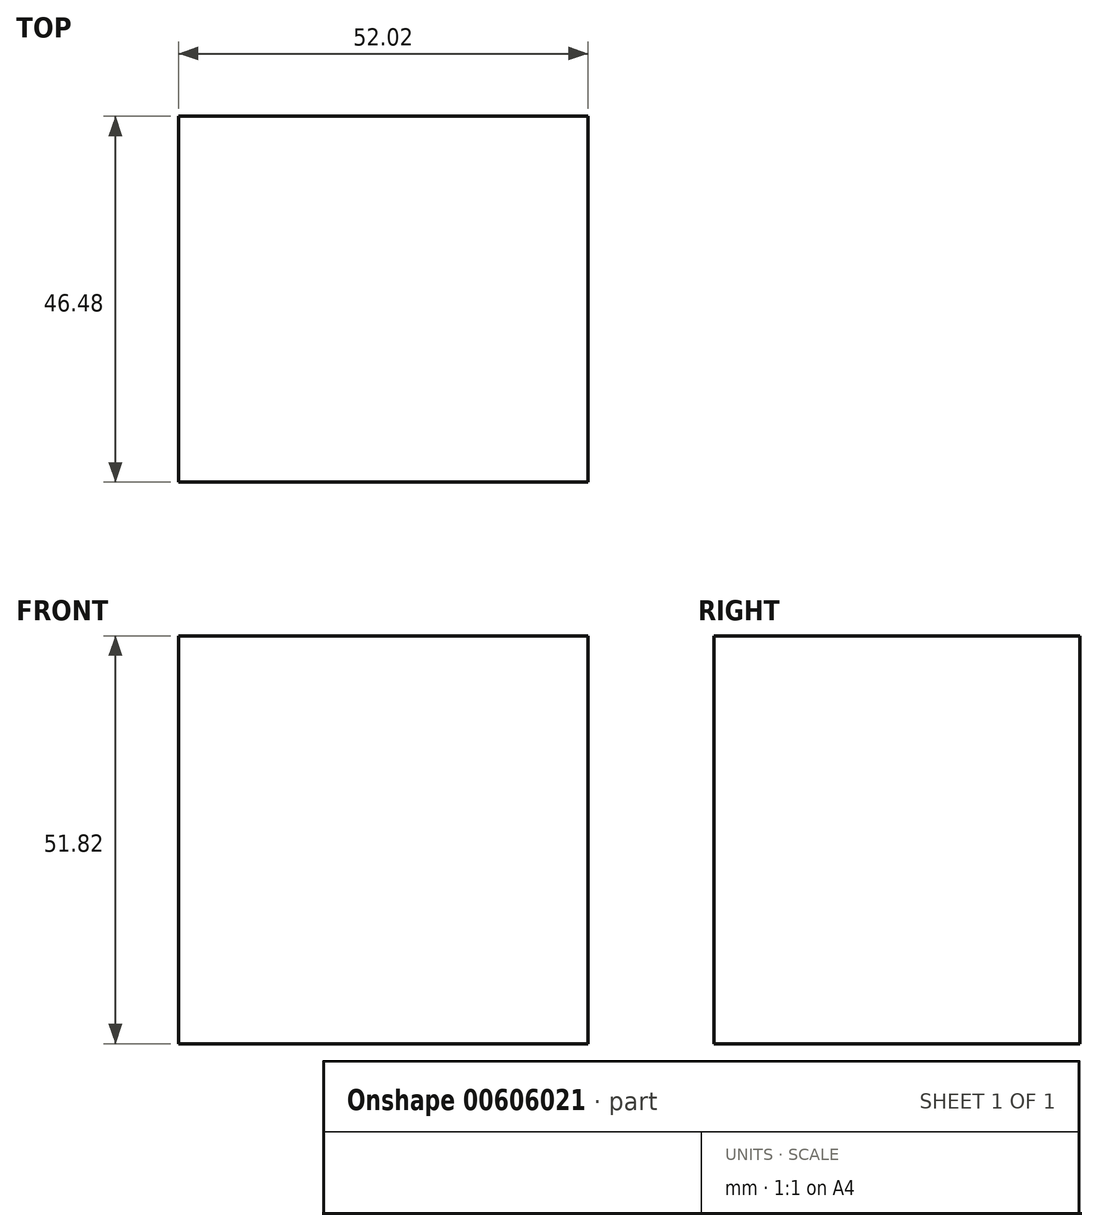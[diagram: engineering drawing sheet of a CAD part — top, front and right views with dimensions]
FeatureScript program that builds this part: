
annotation { "Feature Type Name" : "Feature", "Feature Type Description" : "" }
export const myFeature = defineFeature(function(context is Context, id is Id, definition is map)
    precondition{}
    {
        {
            var Q0;
            Q0=qCreatedBy(makeId("Front.planeOp"),FACE);
            var sketch = newSketch(context, id + "F0", { "sketchPlane" : qUnion([Q0])});
            skLineSegment(sketch, "E0.bottom", {"start": v(-26.15, 25.57) * mm, "end": v(25.87, 25.57) * mm});
            skLineSegment(sketch, "E0.top", {"start": v(-26.15, -26.25) * mm, "end": v(25.87, -26.25) * mm});
            skLineSegment(sketch, "E0.left", {"start": v(-26.15, 25.57) * mm, "end": v(-26.15, -26.25) * mm});
            skLineSegment(sketch, "E0.right", {"start": v(25.87, 25.57) * mm, "end": v(25.87, -26.25) * mm});
            skSolve(sketch);
        }
        {
            var Q0;
            Q0=makeQuery(id+"F0.imprint","IMPRINT",FACE,{"disambiguationData":[TD([[makeQuery(id+"F0.imprint","IMPRINT",EDGE,{"derivedFrom":sQuery(id+"F0.wireOp",EDGE,"E0.bottom")}),-1.0]])]});
            extrude(context, id + "F1", {"entities" : qUnion([Q0]), "depth" : 46.48 * mm, "offsetDistance" : 25.4 * mm});
        }
    });
